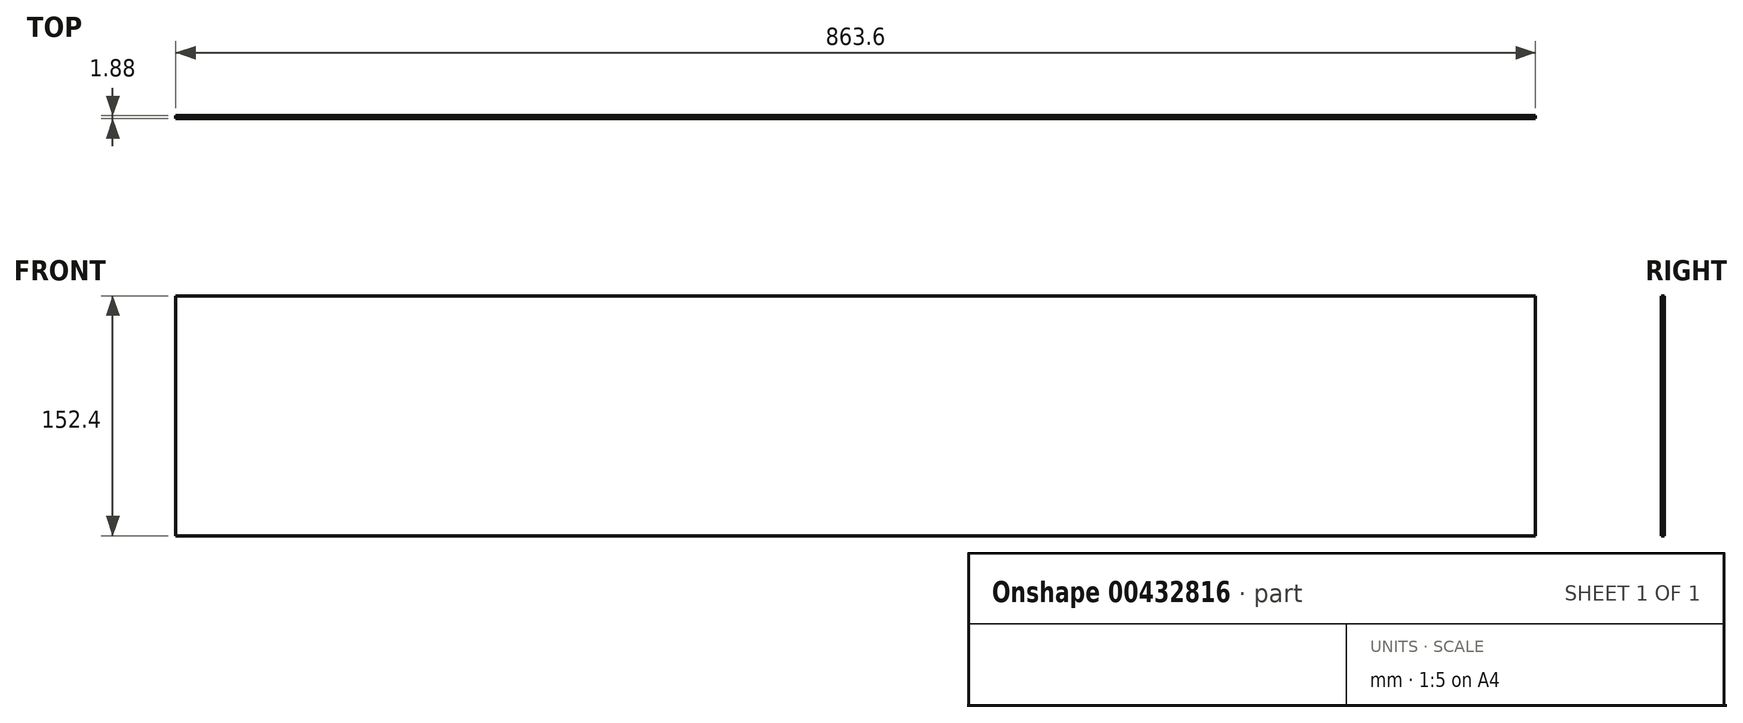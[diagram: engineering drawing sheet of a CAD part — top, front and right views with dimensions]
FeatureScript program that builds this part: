
annotation { "Feature Type Name" : "Feature", "Feature Type Description" : "" }
export const myFeature = defineFeature(function(context is Context, id is Id, definition is map)
    precondition{}
    {
        {
            var Q0;
            Q0=qCreatedBy(makeId("Front.planeOp"),FACE);
            var sketch = newSketch(context, id + "F0", { "sketchPlane" : qUnion([Q0])});
            skLineSegment(sketch, "E0.bottom", {"start": v(431.8, 76.2) * mm, "end": v(-431.8, 76.2) * mm});
            skLineSegment(sketch, "E0.top", {"start": v(431.8, -76.2) * mm, "end": v(-431.8, -76.2) * mm});
            skLineSegment(sketch, "E0.left", {"start": v(431.8, 76.2) * mm, "end": v(431.8, -76.2) * mm});
            skLineSegment(sketch, "E0.right", {"start": v(-431.8, 76.2) * mm, "end": v(-431.8, -76.2) * mm});
            skPoint(sketch, "E0.middle", {"position": v(0, 0) * mm});
            skSolve(sketch);
        }
        {
            var Q0;
            Q0 = qSketchRegion(id + "F0", true);
            extrude(context, id + "F1", {"entities" : qUnion([Q0]), "depth" : 1.88 * mm});
        }
    });
